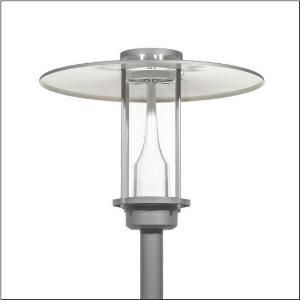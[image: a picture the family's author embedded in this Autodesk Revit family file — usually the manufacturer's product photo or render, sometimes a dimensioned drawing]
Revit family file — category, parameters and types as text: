
# Revit family: city-light_plus_iq___p1_0a_5xa5275nf14hp_e05b
name_source: partatom
category: Lighting Fixtures
units: mm (PartAtom-declared; Revit-internal decimal feet)

## family parameters
Cut with Voids When Loaded = No
Host = Face
Light Source = No
Part Type = Normal
Room Calculation Point = No
Round Connector Dimension = Use Diameter
Shared = No

## types (1)
- --- (1 x LED, 4020 lm, 33.6 W, 2700K)
    Apparent Load = 34 VA
    CIE Flux Codes = 30 60 90 96 100
    Color Rendering = 70
    Color Temperature = 2700K
    Default Elevation = 1800 mm
    Description = City-Light Plus iQ, mast luminaire, Module 540 iQ-SR, primary light control with 3 zone facetted reflector, of plastic, silver coated, highly specular, structured, primary optical cover: cover, of PMMA, transparent, light distribution: P1.0a, light emission: direct distribution, primary light characteristic: strongly asymmetric, installation type: post-top, LED, High Power LED, rated luminous flux: 4.020lm, luminous efficacy: 120lm/W, light colour: 727, colour temperature: 2700K, control gear: ECG iQ, control: presetting dimming logarithmic, Street-Remote, Auto-Match, Temp-Guard, Lumen-Switch, Night-Set, Smart-Wire, Light-Fading, Desk-Remote (wireless, voltage-free reading and setting of iQ features in the workshop via application-optimized NFC function/RFID function), optimised constant luminous flux control (CLO 2.0), with terminal, 6-pole, max. 2.5mm², mains connection: 230..240V, AC, 50/60Hz, start of lifetime: 34W, end of service life: 36W, reduction: 15W, luminaire housing, upper part, of glass-fibre reinforced polyester, coated, Siteco® metallic grey (DB 702S), diameter: 750mm, height: 590mm, spigot size: d x l = 76 x 70mm (post-top) | with reducer (optional accessory) 60 x 70mm, post-top mast mounting element, of diecast aluminium, coated, Siteco® metallic grey (DB 702S), Module 540 iQ-SR, traffic white (RAL 9016), equipment: Power, protection rating (complete): IP65, insulation class (complete): insulation class II (safety insulation), certification: CE, ENEC, VDE, packaging unit: 1 piece

Light Distribution: P1.0a
    Height = 590 mm
    Lamp = 1 x LED
    Lamp Light Flux = 4020 lm
    Lamp Power = 33.6 W
    Lamp count = 1
    Length = 750 mm
    Luminous efficacy = 120 lm/W
    Manufacturer = Siteco
    ModVariant = No
    Model = 5XA5275NF14HP
    Number of Poles = 1
    OnlyDefault = Yes
    Power Factor = 1
    Product Name = City-Light Plus iQ | P1.0a
    Product group = mast luminaire | pylon top
    ProductGroupID = 6100
    Protection Class = Protection class II
    Protection Degree = IP 65
    RLX_Detail_Level = 1
    RLX_Emergency_Light_Flux = 0 lm
    RLX_Emergency_Type = 0
    RLX_Emergency_Type_DB = No
    RlxData = <blob elided: 52613 chars, md5=0d35fb70>
    Socket = socket
    Standby Power = 0 W
    System Light Flux = 4020 lm
    System Power = 34 W
    Type Comments = factory setting: luminous flux: 100 % | dim-lin: 254 | 695 mA
    Type Image = l_1006456.jpg
    URL = http://relux.com
    VarID = @adj_102963
    Voltage = 0 V
    Weight = 0.00 kg
    Width = 0 mm  [stored 0 ft]

note: [stored X ft] marks values corroborated as IEEE doubles in the binary element streams (Revit-internal decimal feet)

## geometry (parser evidence)
native form markers: Blend x4, Sweep x10
no freeform markers — native parametric forms only
